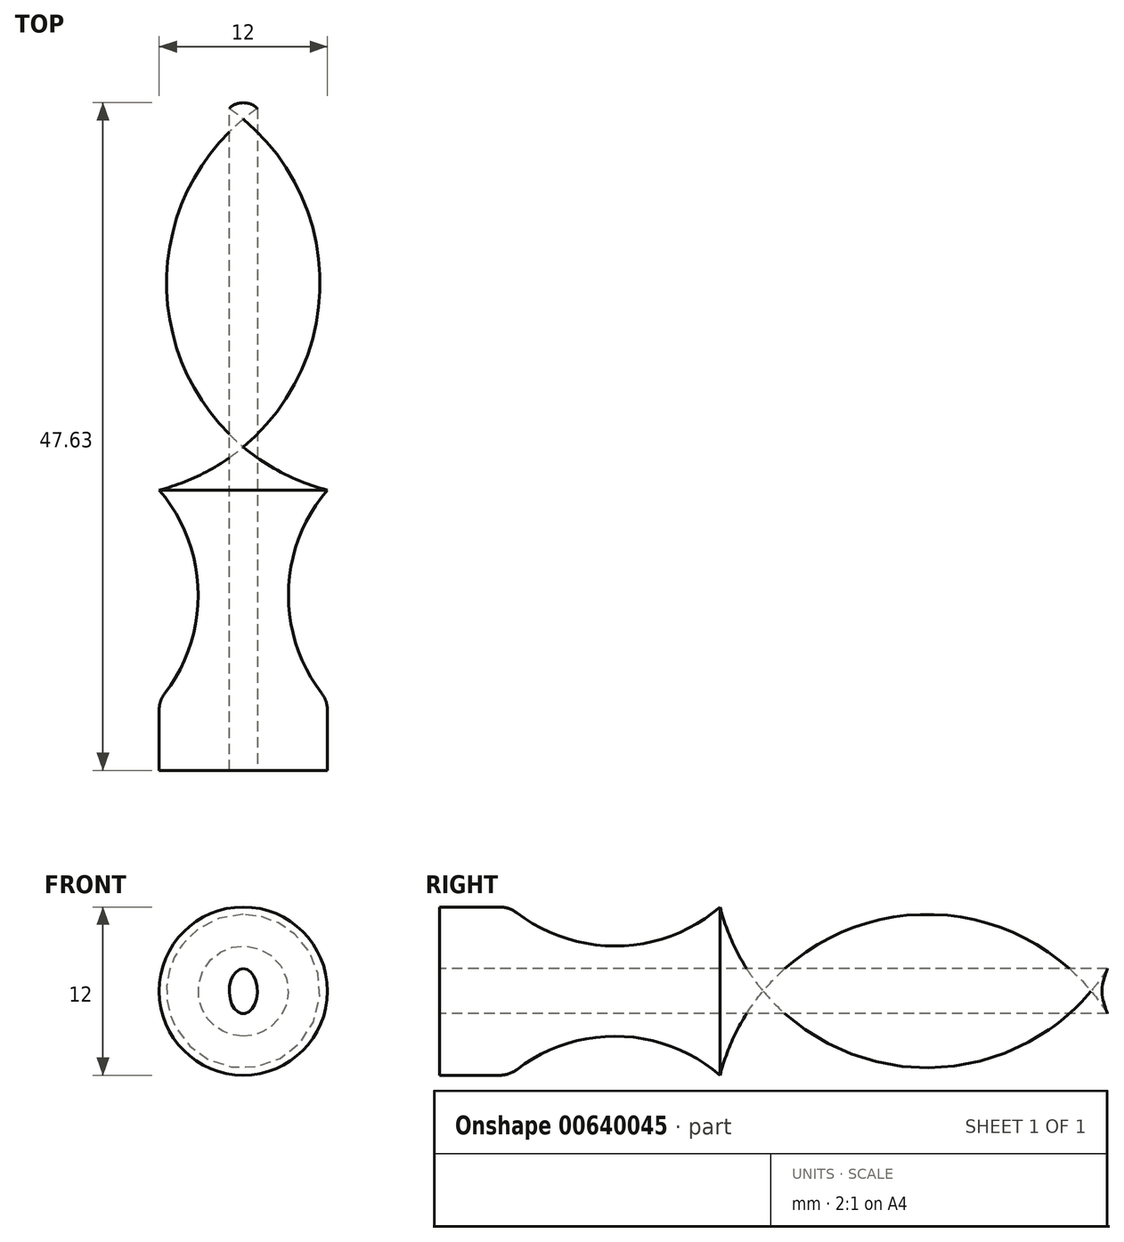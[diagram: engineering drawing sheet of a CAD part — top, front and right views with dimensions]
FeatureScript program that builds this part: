
annotation { "Feature Type Name" : "Feature", "Feature Type Description" : "" }
export const myFeature = defineFeature(function(context is Context, id is Id, definition is map)
    precondition{}
    {
        {
            var Q0;
            Q0=qCreatedBy(makeId("Top.planeOp"),FACE);
            var sketch = newSketch(context, id + "F0", { "sketchPlane" : qUnion([Q0])});
            skLineSegment(sketch, "E0", {"start": v(0, 0) * mm, "end": v(6, 0) * mm});
            skLineSegment(sketch, "E1", {"start": v(0, 0) * mm, "end": v(0, 46.46) * mm});
            skPoint(sketch, "E2.1.internal.snap0", {"position": v(3, 0) * mm});
            skArc(sketch, "E3", {"start": v(6, 20) * mm, "mid": v(24.62, 38.13) * mm, "end": v(0, 46.46) * mm});
            skLineSegment(sketch, "E4", {"start": v(9.76, 50) * mm, "end": v(-8.87, 50) * mm, "construction": true});
            skLineSegment(sketch, "E5", {"start": v(9.76, 50) * mm, "end": v(25.1, 50) * mm, "construction": true});
            skLineSegment(sketch, "E6", {"start": v(6, 0) * mm, "end": v(6, 5) * mm});
            skArc(sketch, "E7", {"start": v(6, 20) * mm, "mid": v(3.22, 12.5) * mm, "end": v(6, 5) * mm});
            skSolve(sketch);
        }
        {
            var Q0;
            Q0 = qSketchRegion(id + "F0", true);
            var Q1;
            Q1=sQuery(id+"F0.wireOp",EDGE,"E1");
            revolve(context, id + "F1", {"surfaceOperationType" : NewSurfaceOperationType.NEW, "entities" : qUnion([Q0]), "axis" : qUnion([Q1]), "revolveType" : RevolveType.FULL});
        }
        {
            var Q0;
            Q0=makeQuery(id+"F1.opRevolve","SWEPT_FACE",FACE,{"disambiguationData":[OSD([sQuery(id+"F0.wireOp",EDGE,"E0")])]});
            var sketch = newSketch(context, id + "F2", { "sketchPlane" : qUnion([Q0])});
            skEllipse(sketch, "E8", {"center": v(0, 0) * mm, "majorRadius": 1 * mm, "minorRadius": 1.6 * mm, "majorAxis": v(1, 0)});
            skSolve(sketch);
        }
        {
            var Q0;
            Q0 = qSketchRegion(id + "F2", true);
            extrude(context, id + "F3", {"entities" : qUnion([Q0]), "operationType" : NewBodyOperationType.REMOVE, "oppositeDirection" : true, "depth" : 55 * mm, "offsetDistance" : 25 * mm});
        }
        {
            var Q0;
            Q0=makeQuery(id+"F1.opRevolve","SWEPT_EDGE",EDGE,{"disambiguationData":[OSD([sQuery(id+"F0.wireOp",EDGE,"E6"),sQuery(id+"F0.wireOp",EDGE,"E7")])]});
            fillet(context, id + "F4", {"entities" : qUnion([Q0]), "tangentPropagation" : true, "radius" : 2 * mm, "defaultsChanged" : true, "vertexSettings" : [], "allowEdgeOverflow" : false});
        }
    });
